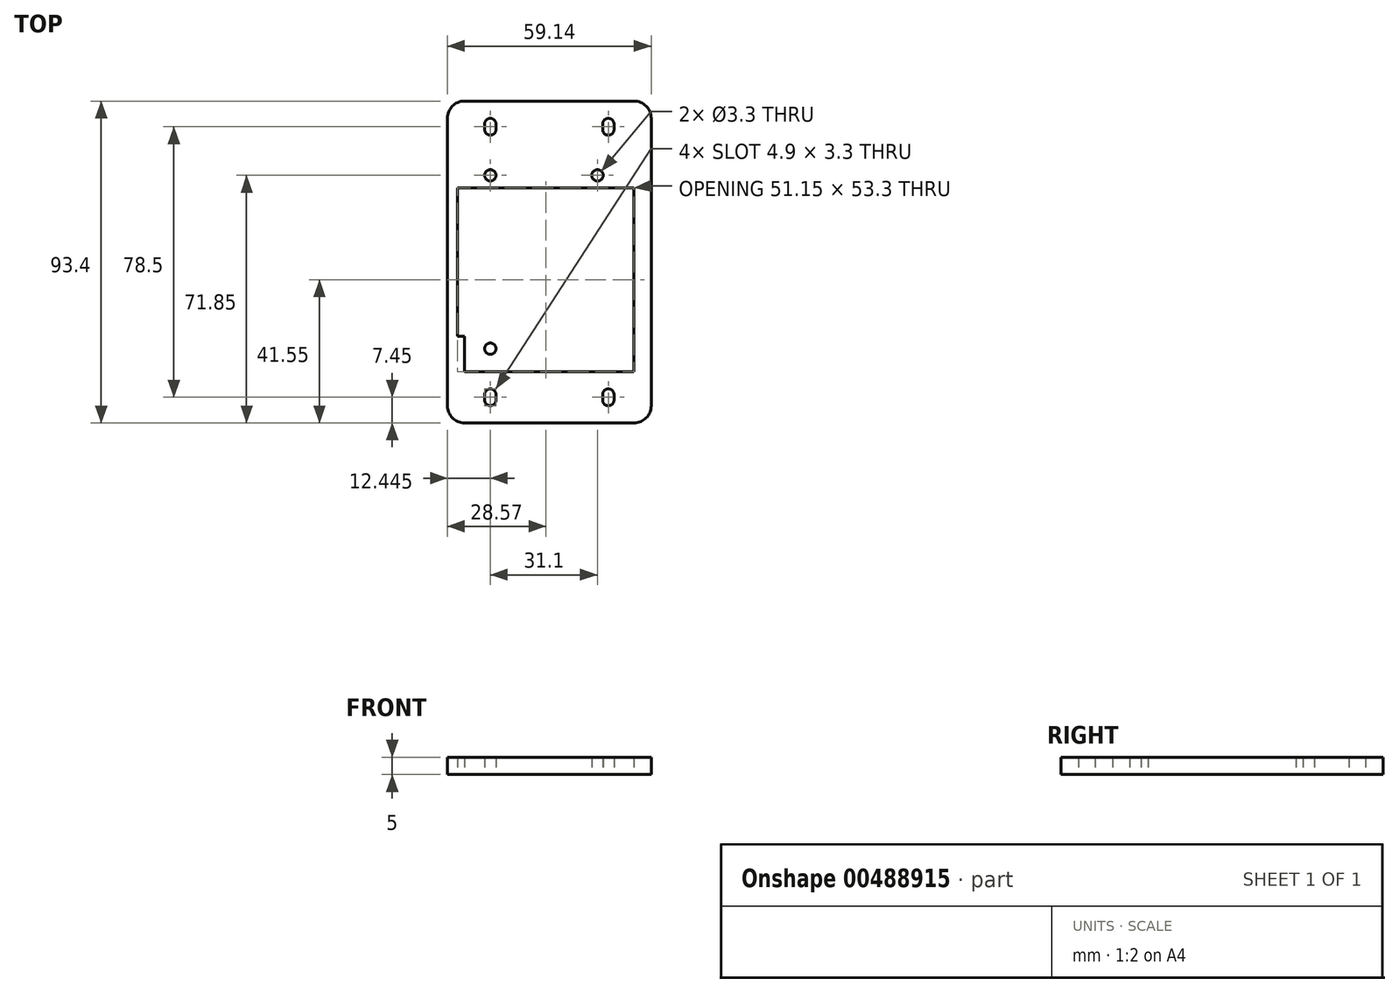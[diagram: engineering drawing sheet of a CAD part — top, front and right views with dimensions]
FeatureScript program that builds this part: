
annotation { "Feature Type Name" : "Feature", "Feature Type Description" : "" }
export const myFeature = defineFeature(function(context is Context, id is Id, definition is map)
    precondition{}
    {
        {
            var Q0;
            Q0=qCreatedBy(makeId("Top.planeOp"),FACE);
            var sketch = newSketch(context, id + "F0", { "sketchPlane" : qUnion([Q0])});
            skLineSegment(sketch, "E0.bottom", {"start": v(-24.57, 31.8) * mm, "end": v(24.58, 31.8) * mm});
            skLineSegment(sketch, "E0.top", {"start": v(-24.58, -31.8) * mm, "end": v(24.57, -31.8) * mm});
            skLineSegment(sketch, "E0.left", {"start": v(-24.57, 31.8) * mm, "end": v(-24.58, -31.8) * mm});
            skLineSegment(sketch, "E0.right", {"start": v(24.58, 31.8) * mm, "end": v(24.57, -31.8) * mm});
            skPoint(sketch, "E0.middle", {"position": v(0, 0) * mm});
            skLineSegment(sketch, "E1.bottom", {"start": v(-24.57, 21.5) * mm, "end": v(24.57, 21.5) * mm});
            skLineSegment(sketch, "E1.top", {"start": v(-24.57, -21.5) * mm, "end": v(24.57, -21.5) * mm});
            skLineSegment(sketch, "E1.left", {"start": v(-24.57, 21.5) * mm, "end": v(-24.57, -21.5) * mm});
            skLineSegment(sketch, "E1.right", {"start": v(24.57, 21.5) * mm, "end": v(24.57, -21.5) * mm});
            skLineSegment(sketch, "E2.bottom", {"start": v(24.58, 31.8) * mm, "end": v(29.57, 31.8) * mm});
            skLineSegment(sketch, "E2.top", {"start": v(24.58, -31.8) * mm, "end": v(29.58, -31.8) * mm});
            skLineSegment(sketch, "E2.left", {"start": v(24.58, 31.8) * mm, "end": v(24.58, -31.8) * mm});
            skLineSegment(sketch, "E2.right", {"start": v(29.57, 31.8) * mm, "end": v(29.58, -31.8) * mm});
            skLineSegment(sketch, "E3.bottom", {"start": v(-24.57, 31.8) * mm, "end": v(-29.58, 31.8) * mm});
            skLineSegment(sketch, "E3.top", {"start": v(-24.57, -31.8) * mm, "end": v(-29.58, -31.8) * mm});
            skLineSegment(sketch, "E3.left", {"start": v(-24.57, 31.8) * mm, "end": v(-24.57, -31.8) * mm});
            skLineSegment(sketch, "E3.right", {"start": v(-29.58, 31.8) * mm, "end": v(-29.58, -31.8) * mm});
            skCircle(sketch, "E4", {"center": v(-17.12, 25.15) * mm, "radius": 1.65 * mm});
            skCircle(sketch, "E5", {"center": v(-17.12, -25.15) * mm, "radius": 1.65 * mm});
            skCircle(sketch, "E6", {"center": v(13.98, -25.15) * mm, "radius": 1.65 * mm});
            skLineSegment(sketch, "E7.bottom", {"start": v(29.57, 31.8) * mm, "end": v(-29.58, 31.8) * mm});
            skLineSegment(sketch, "E7.top", {"start": v(29.57, 46.7) * mm, "end": v(-29.58, 46.7) * mm});
            skLineSegment(sketch, "E7.left", {"start": v(29.57, 31.8) * mm, "end": v(29.57, 46.7) * mm});
            skLineSegment(sketch, "E7.right", {"start": v(-29.58, 31.8) * mm, "end": v(-29.58, 46.7) * mm});
            skCircle(sketch, "E8", {"center": v(17.12, 38.45) * mm, "radius": 1.65 * mm});
            skCircle(sketch, "E9", {"center": v(-17.12, 38.45) * mm, "radius": 1.65 * mm});
            skLineSegment(sketch, "E10", {"start": v(-15.48, 38.45) * mm, "end": v(-18.77, 38.45) * mm});
            skCircle(sketch, "E11", {"center": v(-17.12, 40.05) * mm, "radius": 1.65 * mm});
            skLineSegment(sketch, "E12", {"start": v(-15.48, 40.05) * mm, "end": v(-18.77, 40.05) * mm});
            skLineSegment(sketch, "E13", {"start": v(-18.77, 40.05) * mm, "end": v(-18.77, 38.45) * mm});
            skLineSegment(sketch, "E14", {"start": v(-15.48, 40.05) * mm, "end": v(-15.48, 38.45) * mm});
            skLineSegment(sketch, "E15.MirrorCS", {"start": v(24.58, -31.8) * mm, "end": v(29.57, -31.8) * mm});
            skLineSegment(sketch, "E16.MirrorCS", {"start": v(-15.48, -38.45) * mm, "end": v(-18.77, -38.45) * mm});
            skLineSegment(sketch, "E17.MirrorCS", {"start": v(-18.77, -40.05) * mm, "end": v(-18.77, -38.45) * mm});
            skLineSegment(sketch, "E18.MirrorCS", {"start": v(-15.48, -40.05) * mm, "end": v(-18.77, -40.05) * mm});
            skLineSegment(sketch, "E19.MirrorCS", {"start": v(-15.48, -40.05) * mm, "end": v(-15.48, -38.45) * mm});
            skCircle(sketch, "E20.MirrorC", {"center": v(-17.12, -40.05) * mm, "radius": 1.65 * mm});
            skCircle(sketch, "E21.MirrorC", {"center": v(-17.12, -38.45) * mm, "radius": 1.65 * mm});
            skCircle(sketch, "E22.MirrorC", {"center": v(17.12, -40.05) * mm, "radius": 1.65 * mm});
            skCircle(sketch, "E23.MirrorC", {"center": v(17.12, -38.45) * mm, "radius": 1.65 * mm});
            skLineSegment(sketch, "E24.MirrorCS", {"start": v(-24.57, -31.8) * mm, "end": v(24.58, -31.8) * mm});
            skLineSegment(sketch, "E25.MirrorCS", {"start": v(-29.58, -31.8) * mm, "end": v(-29.58, -46.7) * mm});
            skLineSegment(sketch, "E26.MirrorCS", {"start": v(29.57, -46.7) * mm, "end": v(-29.58, -46.7) * mm});
            skLineSegment(sketch, "E27.MirrorCS", {"start": v(29.57, -31.8) * mm, "end": v(29.57, -46.7) * mm});
            skLineSegment(sketch, "E28.MirrorCS", {"start": v(29.57, -31.8) * mm, "end": v(-29.58, -31.8) * mm});
            skLineSegment(sketch, "E29", {"start": v(18.77, 38.45) * mm, "end": v(15.47, 38.45) * mm});
            skCircle(sketch, "E30", {"center": v(17.12, 40.05) * mm, "radius": 1.65 * mm});
            skLineSegment(sketch, "E31", {"start": v(18.77, 40.05) * mm, "end": v(15.47, 40.05) * mm});
            skLineSegment(sketch, "E32", {"start": v(15.47, 40.05) * mm, "end": v(15.47, 38.45) * mm});
            skLineSegment(sketch, "E33", {"start": v(18.77, 38.45) * mm, "end": v(18.77, 40.05) * mm});
            skLineSegment(sketch, "E34.MirrorCS", {"start": v(18.77, -38.45) * mm, "end": v(18.77, -40.05) * mm});
            skLineSegment(sketch, "E35.MirrorCS", {"start": v(18.77, -38.45) * mm, "end": v(15.47, -38.45) * mm});
            skLineSegment(sketch, "E36.MirrorCS", {"start": v(18.77, -40.05) * mm, "end": v(15.47, -40.05) * mm});
            skLineSegment(sketch, "E37.MirrorCS", {"start": v(15.47, -40.05) * mm, "end": v(15.47, -38.45) * mm});
            skCircle(sketch, "E38.MirrorC", {"center": v(13.98, 25.15) * mm, "radius": 1.65 * mm});
            skLineSegment(sketch, "E39.bottom", {"start": v(-24.57, -21.5) * mm, "end": v(-26.57, -21.5) * mm});
            skLineSegment(sketch, "E39.top", {"start": v(-24.57, 21.5) * mm, "end": v(-26.58, 21.5) * mm});
            skLineSegment(sketch, "E39.left", {"start": v(-24.57, -21.5) * mm, "end": v(-24.57, 21.5) * mm});
            skLineSegment(sketch, "E39.right", {"start": v(-26.57, -21.5) * mm, "end": v(-26.58, 21.5) * mm});
            skSolve(sketch);
        }
        {
            var Q0;
            Q0=makeQuery(id+"F0.imprint","IMPRINT",FACE,{"disambiguationData":[TD([[makeQuery(id+"F0.imprint","IMPRINT",EDGE,{"derivedFrom":sQuery(id+"F0.wireOp",EDGE,"E7.top")}),1.0]])]});
            var Q1;
            {var subQ0=sQuery(id+"F0.wireOp",EDGE,"E2.right");Q1=makeQuery(id+"F0.imprint","IMPRINT",FACE,{"disambiguationData":[TD([[makeQuery(id+"F0.imprint","IMPRINT",EDGE,{"derivedFrom":subQ0}),-1.0]])]});}
            var Q2;
            {var subQ1=sQuery(id+"F0.wireOp",EDGE,"E1.bottom");Q2=makeQuery(id+"F0.imprint","IMPRINT",FACE,{"disambiguationData":[TD([[makeQuery(id+"F0.imprint","IMPRINT",EDGE,{"derivedFrom":subQ1}),1.0]])]});}
            var Q3;
            Q3=makeQuery(id+"F0.imprint","IMPRINT",FACE,{"disambiguationData":[TD([[makeQuery(id+"F0.imprint","IMPRINT",EDGE,{"derivedFrom":sQuery(id+"F0.wireOp",EDGE,"E5")}),1.0]])]});
            var Q4;
            {var subQ0=sQuery(id+"F0.wireOp",EDGE,"E3.right");Q4=makeQuery(id+"F0.imprint","IMPRINT",FACE,{"disambiguationData":[TD([[makeQuery(id+"F0.imprint","IMPRINT",EDGE,{"derivedFrom":subQ0}),1.0]])]});}
            var Q5;
            {var subQ12=sQuery(id+"F0.wireOp",EDGE,"E17.MirrorCS");Q5=makeQuery(id+"F0.imprint","IMPRINT",FACE,{"disambiguationData":[TD([[makeQuery(id+"F0.imprint","IMPRINT",EDGE,{"derivedFrom":subQ12}),1.0]])]});}
            extrude(context, id + "F1", {"entities" : qUnion([Q0, Q1, Q2, Q3, Q4, Q5]), "depth" : 5 * mm});
        }
        {
            var Q0;
            Q0=makeQuery(id+"F1.opExtrude","SWEPT_EDGE",EDGE,{"disambiguationData":[OSD([sQuery(id+"F0.wireOp",EDGE,"E7.top"),sQuery(id+"F0.wireOp",EDGE,"E7.left")])]});
            var Q1;
            Q1=makeQuery(id+"F1.opExtrude","SWEPT_EDGE",EDGE,{"disambiguationData":[OSD([sQuery(id+"F0.wireOp",EDGE,"E7.top"),sQuery(id+"F0.wireOp",EDGE,"E7.right")])]});
            var Q2;
            Q2=makeQuery(id+"F1.opExtrude","SWEPT_EDGE",EDGE,{"disambiguationData":[OSD([sQuery(id+"F0.wireOp",EDGE,"E26.MirrorCS"),sQuery(id+"F0.wireOp",EDGE,"E25.MirrorCS")])]});
            var Q3;
            Q3=makeQuery(id+"F1.opExtrude","SWEPT_EDGE",EDGE,{"disambiguationData":[OSD([sQuery(id+"F0.wireOp",EDGE,"E27.MirrorCS"),sQuery(id+"F0.wireOp",EDGE,"E26.MirrorCS")])]});
            fillet(context, id + "F2", {"entities" : qUnion([Q0, Q1, Q2, Q3]), "radius" : 5 * mm, "tangentPropagation" : true, "allowEdgeOverflow" : false});
        }
    });
